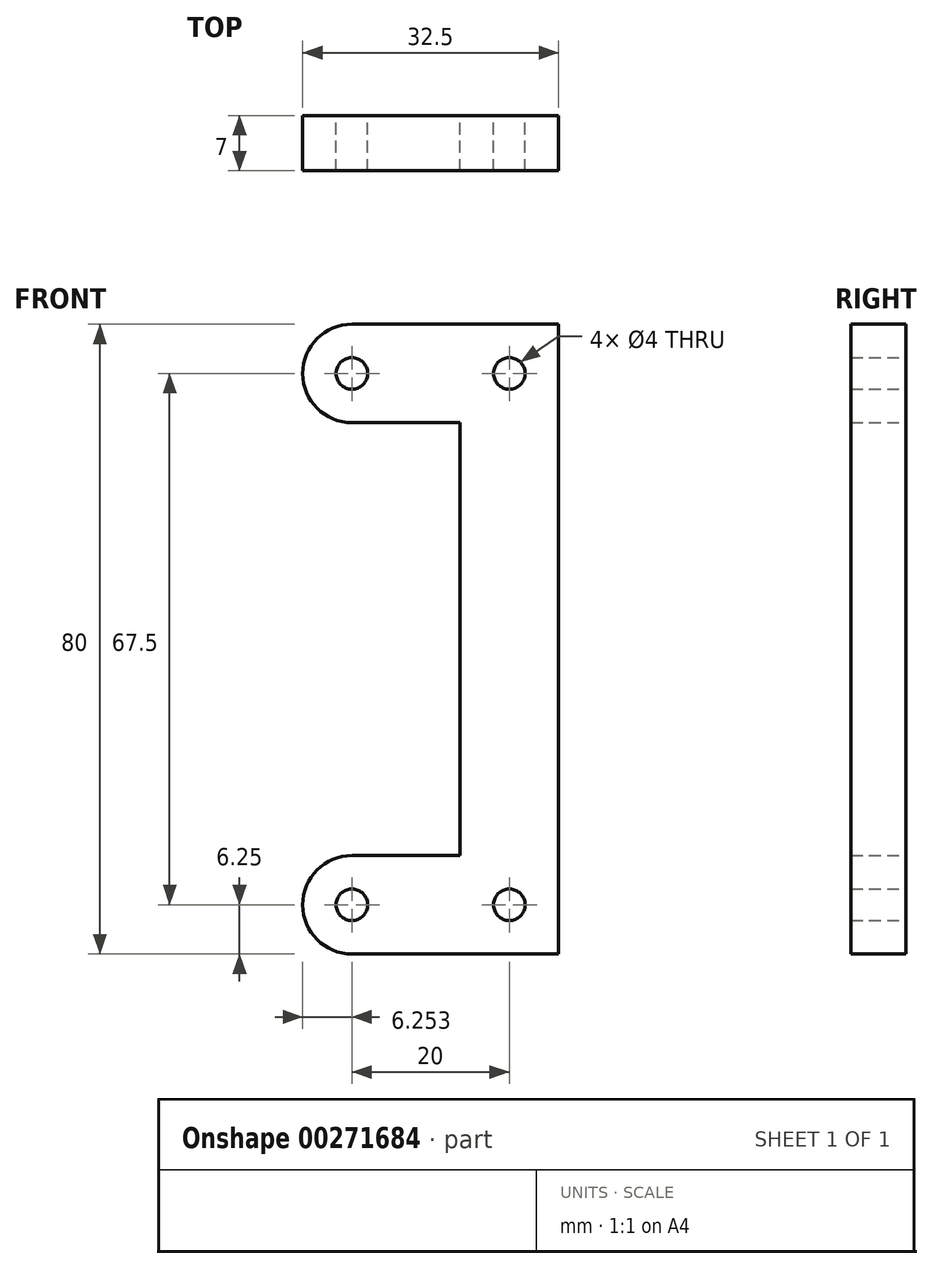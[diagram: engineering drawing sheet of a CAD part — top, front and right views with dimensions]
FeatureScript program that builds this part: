
annotation { "Feature Type Name" : "Feature", "Feature Type Description" : "" }
export const myFeature = defineFeature(function(context is Context, id is Id, definition is map)
    precondition{}
    {
        {
            var Q0;
            Q0=qCreatedBy(makeId("Front.planeOp"),FACE);
            var sketch = newSketch(context, id + "F0", { "sketchPlane" : qUnion([Q0])});
            skLineSegment(sketch, "E0", {"start": v(4.41, -27.5) * mm, "end": v(4.41, 27.5) * mm});
            skLineSegment(sketch, "E1", {"start": v(4.41, 27.5) * mm, "end": v(-9.34, 27.5) * mm});
            skArc(sketch, "E2", {"start": v(-9.34, 40) * mm, "mid": v(-15.59, 33.75) * mm, "end": v(-9.34, 27.5) * mm});
            skLineSegment(sketch, "E3", {"start": v(-9.34, 40) * mm, "end": v(16.91, 40) * mm});
            skLineSegment(sketch, "E4", {"start": v(16.91, 40) * mm, "end": v(16.91, -40) * mm});
            skLineSegment(sketch, "E5", {"start": v(16.91, -40) * mm, "end": v(-9.34, -40) * mm});
            skArc(sketch, "E6", {"start": v(-9.34, -27.5) * mm, "mid": v(-15.59, -33.75) * mm, "end": v(-9.34, -40) * mm});
            skLineSegment(sketch, "E7", {"start": v(-9.34, -27.5) * mm, "end": v(4.41, -27.5) * mm});
            skPoint(sketch, "E8", {"position": v(10.66, 33.75) * mm});
            skPoint(sketch, "E9", {"position": v(10.66, -33.75) * mm});
            skSolve(sketch);
        }
        {
            var Q0;
            Q0=makeQuery(id+"F0.imprint","IMPRINT",FACE,{"disambiguationData":[TD([[makeQuery(id+"F0.imprint","IMPRINT",EDGE,{"derivedFrom":sQuery(id+"F0.wireOp",EDGE,"E0")}),-1.0]])]});
            extrude(context, id + "F1", {"entities" : qUnion([Q0]), "depth" : 7 * mm});
        }
        {
            var Q0;
            Q0=sQuery(id+"F0.wireOp",VERTEX,"E2.center");
            var Q1;
            Q1=sQuery(id+"F0.wireOp",VERTEX,"E8");
            var Q2;
            Q2=sQuery(id+"F0.wireOp",VERTEX,"E6.center");
            var Q3;
            Q3=sQuery(id+"F0.wireOp",VERTEX,"E9");
            var Q4;
            Q4=makeQuery(id+"F1.opExtrude","SWEPT_BODY",BODY,{"disambiguationData":[OSD([sQuery(id+"F0.wireOp",EDGE,"E0"),sQuery(id+"F0.wireOp",EDGE,"E1"),sQuery(id+"F0.wireOp",EDGE,"E2"),sQuery(id+"F0.wireOp",EDGE,"E3"),sQuery(id+"F0.wireOp",EDGE,"E4"),sQuery(id+"F0.wireOp",EDGE,"E5"),sQuery(id+"F0.wireOp",EDGE,"E6"),sQuery(id+"F0.wireOp",EDGE,"E7")])]});
            hole(context, id + "F2", {"style" : HoleStyle.SIMPLE, "endStyle" : HoleEndStyle.THROUGH, "oppositeDirection" : true, "holeDiameter" : 4 * mm, "tappedDepth" : 12 * mm, "tapClearance" : 3, "locations" : qUnion([Q0, Q1, Q2, Q3]), "scope" : qUnion([Q4])});
        }
    });
